# Revit family: Domotics-DomesticRanges-GEWISS-27COMBI_SYSTEM-IP44_SOCKET_OUTLETS_IEC309
name_source: partatom
category: Modelli generici
revit_build: Autodesk Revit 2016 (Build: 20161004_0715(x64)
units: mm (PartAtom-declared; Revit-internal decimal feet)

## family parameters
Condiviso = No
Host = Muro
Punto di calcolo locali = No
Può ospitare armatura = No
Quota connettore circolare = Usa diametro
Sempre verticale = Sì
Taglio con vuoti quando caricato = No
Tipo di parte = Normale

## types (2) — shared parameters
Altezza = 84 mm
Catalogue = DOMOTICS
Catalogue Range = 27COMBI
Colour = Grey RAL 7035
Electrocod = 2210
Finitura = <Per categoria>
Glow Wire Test = 650°C
IDF = b8e11bee-75b0-43ea-8ef5-5655e11cbaa8
IDT = f00df10a-2b06-41cb-b6d5-a9cceb99cd24
IP degree = IP44
Immagine tipo = GW26421.jpg
Installation temperature = -25 +60 °C
Insulation class = II
Larghezza = 116 mm  [stored 0.380577 ft]
Outer dim. LxHxD (mm) = 116x90x45
Produttore = GEWISS S.p.A.
Profondità = 45 mm  [stored 0.147638 ft]
Rated current (In) = 16
Reference h = 6
Standard = IEC 309
Technical sheet = https://www.gewiss.com
Thermo-pressure with ball = 70
URL = https://www.gewiss.com
Version file RFA = 18.0
leva = <Per categoria>

## per-type parameters (varying)
| type | Descrizione | EAN code | Modello | Number of poles | Rated voltage |
| GW26420 - 16a 2P+E 220V IEC309 socket outlet | 16A 2P+E 220V IEC309 SOCKET OUTLET | 8011564025448 | GW26420 | 2P+E | 230V ac |
| GW26421 - 16a 3P+E 380V IEC309 socket outlet | 16A 3P+E 380V IEC309 SOCKET OUTLET | 8011564025431 | GW26421 | 3P+E | 400V ac |

note: source unit labels omitted for Thermo-pressure with ball — the stored unit's dimension contradicts the parameter name (converter mislabeling)

note: [stored X ft] marks values corroborated as IEEE doubles in the binary element streams (Revit-internal decimal feet)
